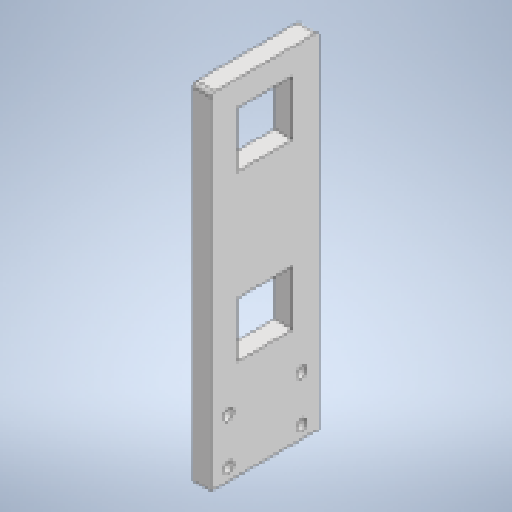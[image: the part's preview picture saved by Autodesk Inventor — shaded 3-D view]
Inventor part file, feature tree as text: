
AUTODESK INVENTOR PART (.ipt)
format: ipt  version: 2023 (Build 270158000, 158)  size: 166,912 bytes
history: native  units: mm
features: extrude x2, sketch x2
ambient origin geometry x8: Origin, YZ Plane, XZ Plane, XY Plane, X Axis, Y Axis, Z Axis, Center Point
bodies: Solid1 (feature_tree)
feature tree (4):
  extrude  "Extrusion1"  Depth=25.0mm
  extrude  "Extrusion2"  Depth=58.8mm
  sketch  "Sketch1"  dims[d0=6.0mm d1=25.0mm]
  sketch  "Sketch3"  dims[d2=40.0mm d3=58.8mm d4=38.2mm d5=10.0mm d6=0.0mm d7=150.0mm d8=2.0mm d9=30.0mm d12=60.0mm d13=16.0mm d14=10.0mm d15=0.0mm]
